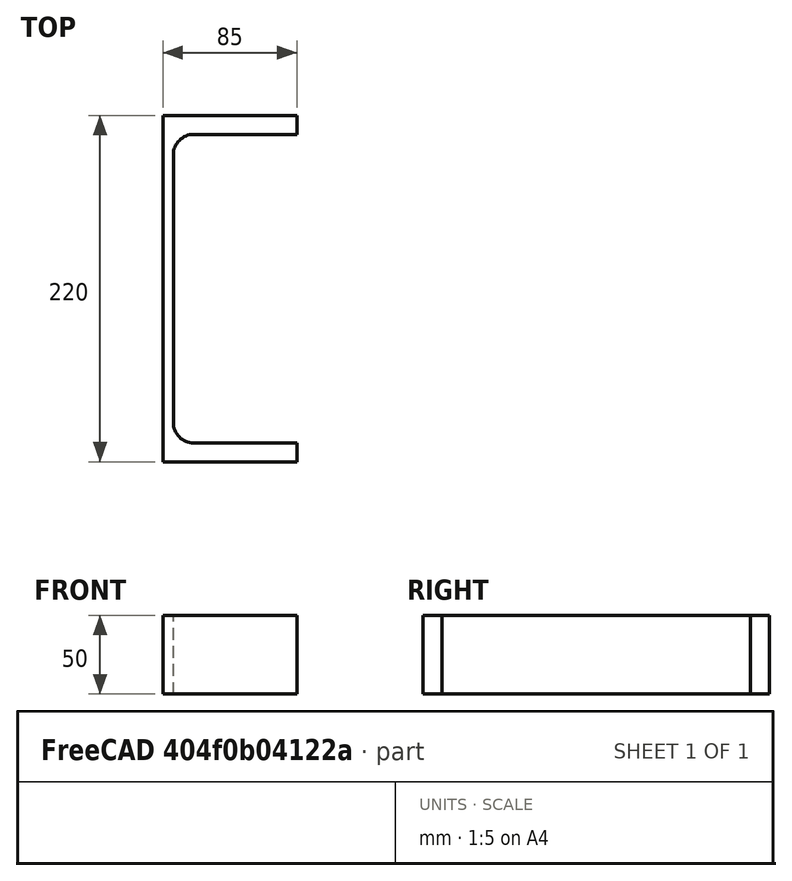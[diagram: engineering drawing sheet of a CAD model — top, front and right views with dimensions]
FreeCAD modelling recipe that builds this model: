
FCSTD DOCUMENT  (FreeCAD 0.20R29410 (Git))
Label: UPE-Profile 220 DIN1026-2 S235JR
License: All rights reserved
LicenseURL: http://en.wikipedia.org/wiki/All_rights_reserved
objects: Sketcher::SketchObject×1, Part::Extrusion×1
note: 2 computed .brp shape members not serialized (recipe doc carries the construction recipe); baked Part::Feature solids carry a one-line shape summary decoded from their .brp

FEATURE [Sketcher::SketchObject] Sketch
  FullyConstrained = true
  MapMode = 5
  sketch-geometry (10):
    g0: LineSegment StartX=6.5 StartY=-85 StartZ=0 EndX=6.5 EndY=85 EndZ=0
    g1: LineSegment StartX=19.5 StartY=98 StartZ=0 EndX=85 EndY=98 EndZ=0
    g2: LineSegment StartX=85 StartY=98 StartZ=0 EndX=85 EndY=110 EndZ=0
    g3: LineSegment StartX=85 StartY=-110 StartZ=0 EndX=85 EndY=-98 EndZ=0
    g4: LineSegment StartX=85 StartY=-98 StartZ=0 EndX=19.5 EndY=-98 EndZ=0
    g5: ArcOfCircle CenterX=19.5 CenterY=85 CenterZ=0 NormalX=0 NormalY=0 NormalZ=1 AngleXU=0 Radius=13 StartAngle=1.5708 EndAngle=3.14159
    g6: ArcOfCircle CenterX=19.5 CenterY=-85 CenterZ=0 NormalX=0 NormalY=0 NormalZ=1 AngleXU=0 Radius=13 StartAngle=3.14159 EndAngle=4.71239
    g7: LineSegment StartX=85 StartY=-110 StartZ=0 EndX=0 EndY=-110 EndZ=0
    g8: LineSegment StartX=0 StartY=-110 StartZ=0 EndX=0 EndY=110 EndZ=0
    g9: LineSegment StartX=0 StartY=110 StartZ=0 EndX=85 EndY=110 EndZ=0
  constraints (27):
    c: Vertical(g0)
    c: Coincident(g2,g1)
    c: Vertical(g2)
    c: Vertical(g3)
    c: Coincident(g4,g3)
    c: Horizontal(g4)
    c: Tangent(g1,g5) = 1.5708
    c: Tangent(g0,g5) = 1.5708
    c: Tangent(g0,g6) = 1.5708
    c: Tangent(g4,g6) = 1.5708
    c: Symmetric(g2,g3,g-1)
    c: DistanceY(g2) = 12
    c: Radius(g5) = 13
    c: Coincident(g3,g7)
    c: PointOnObject(g7,g-2)
    c: Horizontal(g7)
    c: Coincident(g7,g8)
    c: PointOnObject(g8,g-2)
    c: Coincident(g8,g9)
    c: Coincident(g9,g2)
    c: Horizontal(g9)
    c: Distance(g-1,g0) = 6.5
    c: DistanceX(g9,g9) = 85
    c: Horizontal(g1)
    c: Equal(g3,g2)
    c: Equal(g5,g6)
    c: DistanceY(g3,g2) = 220
FEATURE [Part::Extrusion] Extrude  label="UPE-Profile 220 DIN1026-2 S235JR"
  Base = -> Sketch
  Dir = (0,0,50)
  DirMode = 0
  FaceMakerClass = Part::FaceMakerExtrusion
  LengthFwd = 0
  LengthRev = 0
  Solid = true
  Symmetric = false
